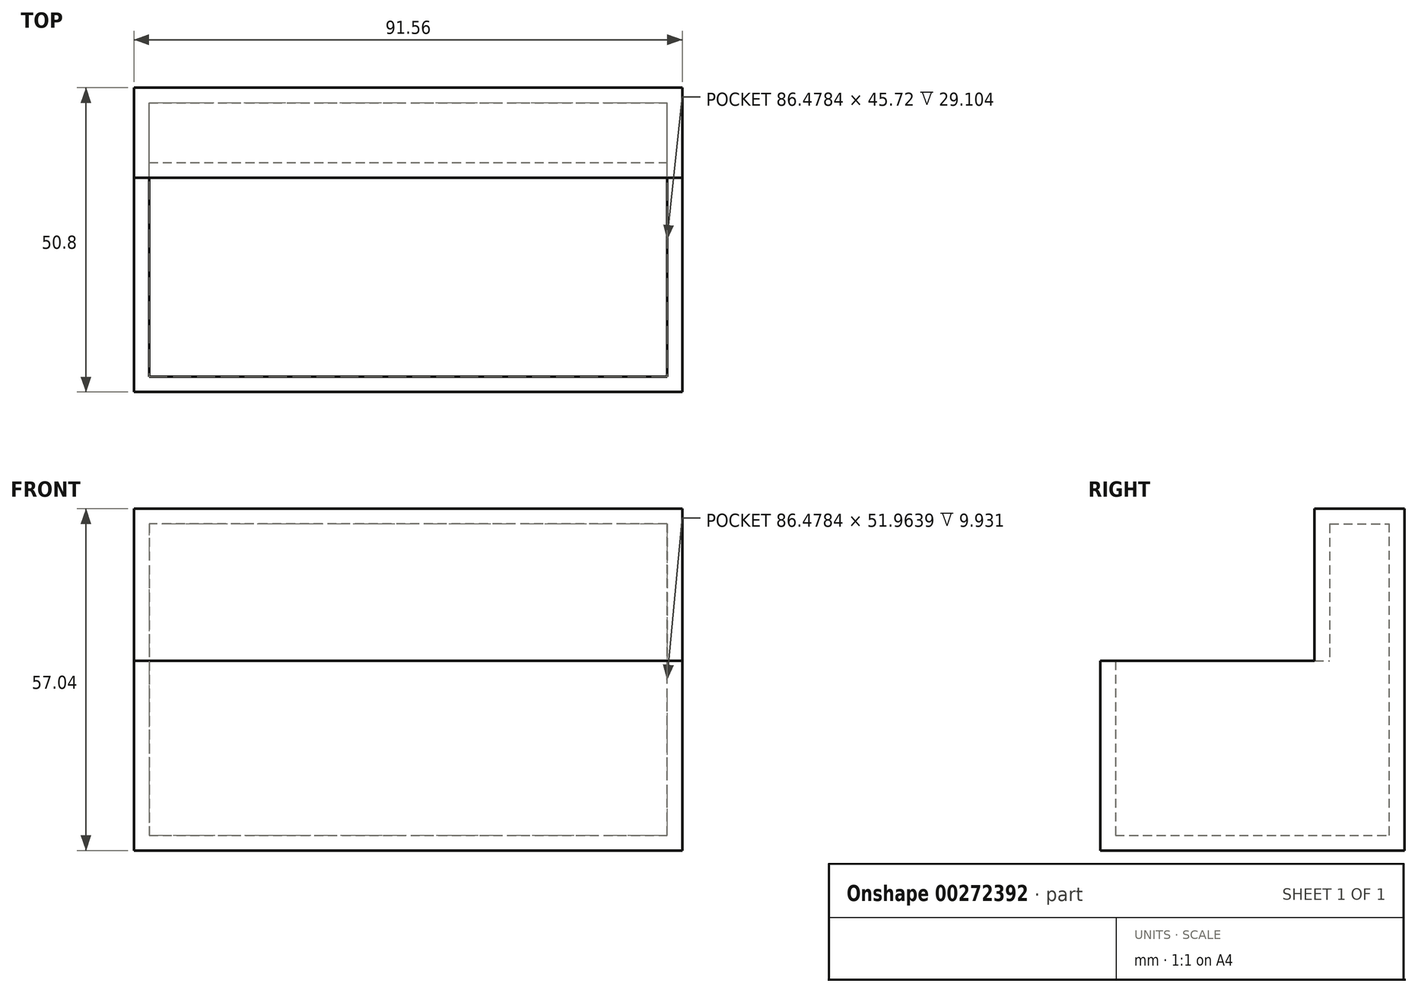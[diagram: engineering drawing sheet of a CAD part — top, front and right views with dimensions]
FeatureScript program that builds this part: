
annotation { "Feature Type Name" : "Feature", "Feature Type Description" : "" }
export const myFeature = defineFeature(function(context is Context, id is Id, definition is map)
    precondition{}
    {
        {
            var Q0;
            Q0=qCreatedBy(makeId("Front.planeOp"),FACE);
            var sketch = newSketch(context, id + "F0", { "sketchPlane" : qUnion([Q0])});
            skLineSegment(sketch, "E0", {"start": v(-52.48, 16.72) * mm, "end": v(-52.48, -14.92) * mm});
            skLineSegment(sketch, "E1", {"start": v(-52.48, -14.92) * mm, "end": v(56.86, -14.92) * mm});
            skLineSegment(sketch, "E2", {"start": v(56.86, -14.92) * mm, "end": v(56.86, 16.72) * mm});
            skLineSegment(sketch, "E3", {"start": v(56.86, 16.72) * mm, "end": v(-52.48, 16.72) * mm});
            skSolve(sketch);
        }
        {
            var Q0;
            Q0=makeQuery(id+"F0.imprint","IMPRINT",FACE,{"disambiguationData":[TD([[makeQuery(id+"F0.imprint","IMPRINT",EDGE,{"derivedFrom":sQuery(id+"F0.wireOp",EDGE,"E0")}),1.0]])]});
            extrude(context, id + "F1", {"entities" : qUnion([Q0]), "depth" : 50.8 * mm});
        }
        {
            var Q0;
            Q0=makeQuery(id+"F1.opExtrude","SWEPT_FACE",FACE,{"disambiguationData":[OSD([sQuery(id+"F0.wireOp",EDGE,"E3")])]});
            var sketch = newSketch(context, id + "F2", { "sketchPlane" : qUnion([Q0])});
            skLineSegment(sketch, "E4", {"start": v(-52.48, -15.01) * mm, "end": v(56.86, -15.01) * mm});
            skLineSegment(sketch, "E5", {"start": v(56.86, -15.01) * mm, "end": v(56.86, 0) * mm});
            skLineSegment(sketch, "E6", {"start": v(56.86, 0) * mm, "end": v(-52.48, 0) * mm});
            skLineSegment(sketch, "E7", {"start": v(-52.48, 0) * mm, "end": v(-52.48, -15.01) * mm});
            skSolve(sketch);
        }
        {
            var Q0;
            Q0=makeQuery(id+"F2.imprint","IMPRINT",FACE,{"disambiguationData":[TD([[makeQuery(id+"F2.imprint","IMPRINT",EDGE,{"derivedFrom":sQuery(id+"F2.wireOp",EDGE,"E4")}),1.0]])]});
            extrude(context, id + "F3", {"entities" : qUnion([Q0]), "operationType" : NewBodyOperationType.ADD, "depth" : 25.4 * mm});
        }
        {
            var Q0;
            Q0=makeQuery(id+"F3.boolean.opBoolean","MERGE",FACE,{"derivedFrom":[makeQuery(id+"F1.opExtrude","SWEPT_FACE",FACE,{"disambiguationData":[OSD([sQuery(id+"F0.wireOp",EDGE,"E2")])]}),makeQuery(id+"F3.opExtrude","SWEPT_FACE",FACE,{"disambiguationData":[OSD([sQuery(id+"F2.wireOp",EDGE,"E5")])]})]});
            extrude(context, id + "F4", {"entities" : qUnion([Q0]), "operationType" : NewBodyOperationType.REMOVE, "oppositeDirection" : true, "depth" : 17.78 * mm});
        }
        {
            var Q0;
            Q0=makeQuery(id+"F1.opExtrude","SWEPT_FACE",FACE,{"disambiguationData":[OSD([sQuery(id+"F0.wireOp",EDGE,"E3")])]});
            shell(context, id + "F5", {"entities" : qUnion([Q0]), "thickness" : 2.54 * mm});
        }
    });
